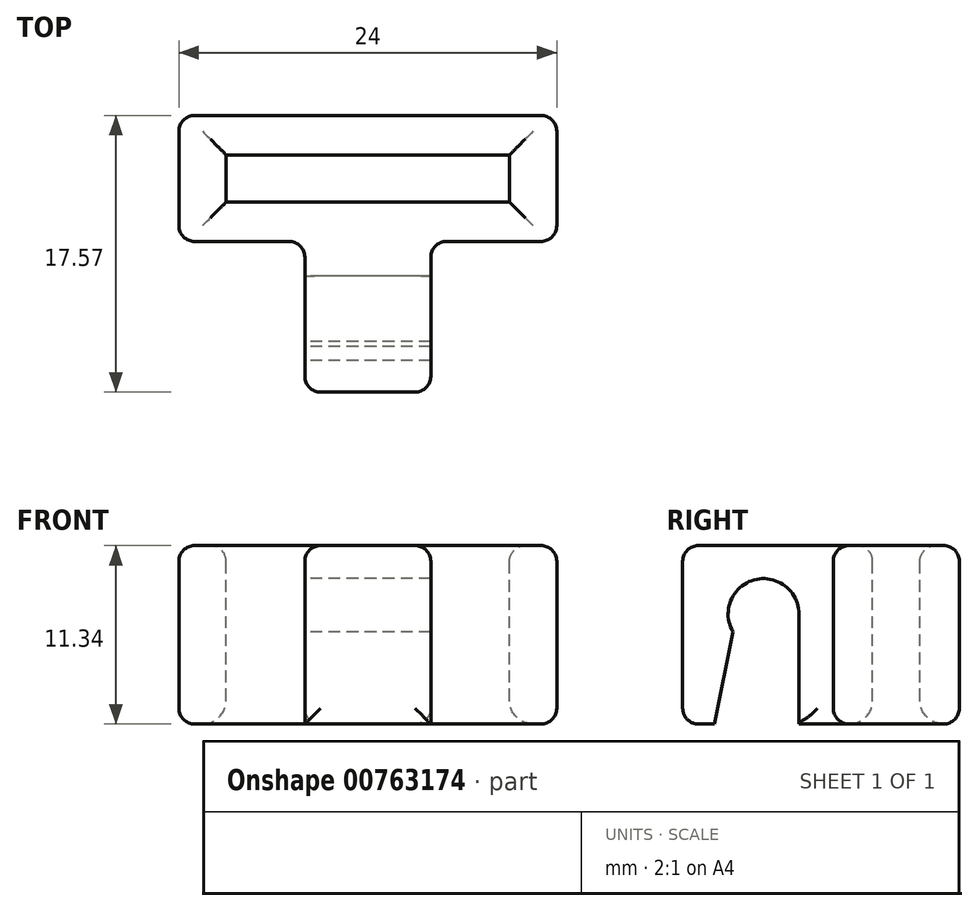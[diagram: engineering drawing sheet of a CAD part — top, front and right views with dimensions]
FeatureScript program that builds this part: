
annotation { "Feature Type Name" : "Feature", "Feature Type Description" : "" }
export const myFeature = defineFeature(function(context is Context, id is Id, definition is map)
    precondition{}
    {
        {
            var Q0;
            Q0=qCreatedBy(makeId("Right.planeOp"),FACE);
            var sketch = newSketch(context, id + "F0", { "sketchPlane" : qUnion([Q0])});
            skArc(sketch, "E0", {"start": v(-16.42, 11.9) * mm, "mid": v(-19.26, 14.08) * mm, "end": v(-20.6, 10.76) * mm});
            skLineSegment(sketch, "E1", {"start": v(-16.42, 11.9) * mm, "end": v(-16.42, 4.92) * mm});
            skLineSegment(sketch, "E2", {"start": v(-20.6, 10.76) * mm, "end": v(-21.78, 4.92) * mm});
            skLineSegment(sketch, "E3", {"start": v(-16.42, 4.92) * mm, "end": v(-14.23, 4.92) * mm});
            skLineSegment(sketch, "E4", {"start": v(-14.23, 4.92) * mm, "end": v(-14.23, 16.26) * mm});
            skLineSegment(sketch, "E5", {"start": v(-14.23, 16.26) * mm, "end": v(-23.8, 16.26) * mm});
            skLineSegment(sketch, "E6", {"start": v(-23.8, 16.26) * mm, "end": v(-23.8, 4.92) * mm});
            skLineSegment(sketch, "E7", {"start": v(-23.8, 4.92) * mm, "end": v(-21.78, 4.92) * mm});
            skSolve(sketch);
        }
        {
            var Q0;
            Q0=makeQuery(id+"F0.imprint","IMPRINT",FACE,{"disambiguationData":[TD([[makeQuery(id+"F0.imprint","IMPRINT",EDGE,{"derivedFrom":sQuery(id+"F0.wireOp",EDGE,"E0")}),-1.0]])]});
            extrude(context, id + "F1", {"entities" : qUnion([Q0]), "depth" : 8 * mm, "offsetDistance" : 25 * mm});
        }
        {
            var Q0;
            Q0=makeQuery(id+"F1.opExtrude","SWEPT_FACE",FACE,{"disambiguationData":[OSD([sQuery(id+"F0.wireOp",EDGE,"E4")])]});
            var sketch = newSketch(context, id + "F2", { "sketchPlane" : qUnion([Q0])});
            skLineSegment(sketch, "E8", {"start": v(-16, 4.92) * mm, "end": v(-16, 16.26) * mm});
            skLineSegment(sketch, "E9", {"start": v(-16, 16.26) * mm, "end": v(8, 16.26) * mm});
            skLineSegment(sketch, "E10", {"start": v(8, 16.26) * mm, "end": v(8, 4.92) * mm});
            skLineSegment(sketch, "E11", {"start": v(-16, 4.92) * mm, "end": v(8, 4.92) * mm});
            skSolve(sketch);
        }
        {
            var Q0;
            Q0 = qSketchRegion(id + "F2", true);
            extrude(context, id + "F3", {"entities" : qUnion([Q0]), "operationType" : NewBodyOperationType.ADD, "depth" : 8 * mm, "offsetDistance" : 25 * mm});
        }
        {
            var Q0;
            Q0=makeQuery(id+"F3.boolean.opBoolean","MERGE",FACE,{"derivedFrom":[makeQuery(id+"F1.opExtrude","SWEPT_FACE",FACE,{"disambiguationData":[OSD([sQuery(id+"F0.wireOp",EDGE,"E5")])]}),makeQuery(id+"F3.opExtrude","SWEPT_FACE",FACE,{"disambiguationData":[OSD([sQuery(id+"F2.wireOp",EDGE,"E9")])]})]});
            var sketch = newSketch(context, id + "F4", { "sketchPlane" : qUnion([Q0])});
            skLineSegment(sketch, "E12", {"start": v(13, -11.73) * mm, "end": v(13, -8.73) * mm});
            skLineSegment(sketch, "E13", {"start": v(13, -8.73) * mm, "end": v(-5, -8.73) * mm});
            skLineSegment(sketch, "E14", {"start": v(-5, -8.73) * mm, "end": v(-5, -11.73) * mm});
            skLineSegment(sketch, "E15", {"start": v(-5, -11.73) * mm, "end": v(13, -11.73) * mm});
            skSolve(sketch);
        }
        {
            var Q0;
            Q0=makeQuery(id+"F4.imprint","IMPRINT",FACE,{"disambiguationData":[TD([[makeQuery(id+"F4.imprint","IMPRINT",EDGE,{"derivedFrom":sQuery(id+"F4.wireOp",EDGE,"E12")}),1.0]])]});
            extrude(context, id + "F5", {"entities" : qUnion([Q0]), "operationType" : NewBodyOperationType.REMOVE, "endBound" : BoundingType.THROUGH_ALL, "oppositeDirection" : true, "depth" : 25 * mm, "offsetDistance" : 25 * mm});
        }
        {
            var Q0;
            Q0=makeQuery(id+"F3.boolean.opBoolean","MERGE",FACE,{"derivedFrom":[makeQuery(id+"F1.opExtrude","SWEPT_FACE",FACE,{"disambiguationData":[OSD([sQuery(id+"F0.wireOp",EDGE,"E5")])]}),makeQuery(id+"F3.opExtrude","SWEPT_FACE",FACE,{"disambiguationData":[OSD([sQuery(id+"F2.wireOp",EDGE,"E9")])]})]});
            var Q1;
            Q1=makeQuery(id+"F3.opExtrude","SWEPT_FACE",FACE,{"disambiguationData":[OSD([sQuery(id+"F2.wireOp",EDGE,"E8")])]});
            var Q2;
            Q2=makeQuery(id+"F3.opExtrude","CAP_FACE",FACE,{"disambiguationData":[OSD([sQuery(id+"F2.wireOp",EDGE,"E8"),sQuery(id+"F2.wireOp",EDGE,"E9"),sQuery(id+"F2.wireOp",EDGE,"E10"),sQuery(id+"F2.wireOp",EDGE,"E11")])],"isStart":false});
            var Q3;
            Q3=makeQuery(id+"F3.opExtrude","SWEPT_FACE",FACE,{"disambiguationData":[OSD([sQuery(id+"F2.wireOp",EDGE,"E10")])]});
            var Q4;
            {var subQ2=sQuery(id+"F2.wireOp",EDGE,"E10");var subQ3=sQuery(id+"F2.wireOp",EDGE,"E9");var subQ4=sQuery(id+"F2.wireOp",EDGE,"E11");Q4=makeQuery(id+"F3.boolean.opBoolean","SPLIT",FACE,{"disambiguationData":[TD([makeQuery(id+"F3.opExtrude","SWEPT_FACE",FACE,{"disambiguationData":[OSD([subQ2])]})])],"derivedFrom":makeQuery(id+"F3.opExtrude","CAP_FACE",FACE,{"disambiguationData":[OSD([sQuery(id+"F2.wireOp",EDGE,"E8"),subQ3,subQ2,subQ4])],"isStart":true})});}
            var Q5;
            {var subQ0=sQuery(id+"F2.wireOp",EDGE,"E8");var subQ3=sQuery(id+"F2.wireOp",EDGE,"E9");var subQ4=sQuery(id+"F2.wireOp",EDGE,"E11");Q5=makeQuery(id+"F3.boolean.opBoolean","SPLIT",FACE,{"disambiguationData":[TD([makeQuery(id+"F3.opExtrude","SWEPT_FACE",FACE,{"disambiguationData":[OSD([subQ0])]})])],"derivedFrom":makeQuery(id+"F3.opExtrude","CAP_FACE",FACE,{"disambiguationData":[OSD([subQ0,subQ3,sQuery(id+"F2.wireOp",EDGE,"E10"),subQ4])],"isStart":true})});}
            var Q6;
            Q6=makeQuery(id+"F1.opExtrude","SWEPT_FACE",FACE,{"disambiguationData":[OSD([sQuery(id+"F0.wireOp",EDGE,"E6")])]});
            fillet(context, id + "F6", {"entities" : qUnion([Q0, Q1, Q2, Q3, Q4, Q5, Q6]), "radius" : 1 * mm, "tangentPropagation" : true, "allowEdgeOverflow" : false});
        }
        {
            var Q0;
            Q0=makeQuery(id+"F5.boolean.opBoolean","INTERSECT",EDGE,{"derivedFrom":[makeQuery(id+"F3.boolean.opBoolean","MERGE",FACE,{"derivedFrom":[makeQuery(id+"F1.opExtrude","SWEPT_FACE",FACE,{"disambiguationData":[OSD([sQuery(id+"F0.wireOp",EDGE,"E3")])]}),makeQuery(id+"F3.opExtrude","SWEPT_FACE",FACE,{"disambiguationData":[OSD([sQuery(id+"F2.wireOp",EDGE,"E11")])]})]}),makeQuery(id+"F5.opExtrude","SWEPT_FACE",FACE,{"disambiguationData":[OSD([sQuery(id+"F4.wireOp",EDGE,"E14")])]})]});
            var Q1;
            Q1=makeQuery(id+"F5.boolean.opBoolean","INTERSECT",EDGE,{"derivedFrom":[makeQuery(id+"F3.boolean.opBoolean","MERGE",FACE,{"derivedFrom":[makeQuery(id+"F1.opExtrude","SWEPT_FACE",FACE,{"disambiguationData":[OSD([sQuery(id+"F0.wireOp",EDGE,"E3")])]}),makeQuery(id+"F3.opExtrude","SWEPT_FACE",FACE,{"disambiguationData":[OSD([sQuery(id+"F2.wireOp",EDGE,"E11")])]})]}),makeQuery(id+"F5.opExtrude","SWEPT_FACE",FACE,{"disambiguationData":[OSD([sQuery(id+"F4.wireOp",EDGE,"E15")])]})]});
            var Q2;
            Q2=makeQuery(id+"F5.boolean.opBoolean","INTERSECT",EDGE,{"derivedFrom":[makeQuery(id+"F3.boolean.opBoolean","MERGE",FACE,{"derivedFrom":[makeQuery(id+"F1.opExtrude","SWEPT_FACE",FACE,{"disambiguationData":[OSD([sQuery(id+"F0.wireOp",EDGE,"E3")])]}),makeQuery(id+"F3.opExtrude","SWEPT_FACE",FACE,{"disambiguationData":[OSD([sQuery(id+"F2.wireOp",EDGE,"E11")])]})]}),makeQuery(id+"F5.opExtrude","SWEPT_FACE",FACE,{"disambiguationData":[OSD([sQuery(id+"F4.wireOp",EDGE,"E13")])]})]});
            var Q3;
            Q3=makeQuery(id+"F5.boolean.opBoolean","INTERSECT",EDGE,{"derivedFrom":[makeQuery(id+"F3.boolean.opBoolean","MERGE",FACE,{"derivedFrom":[makeQuery(id+"F1.opExtrude","SWEPT_FACE",FACE,{"disambiguationData":[OSD([sQuery(id+"F0.wireOp",EDGE,"E3")])]}),makeQuery(id+"F3.opExtrude","SWEPT_FACE",FACE,{"disambiguationData":[OSD([sQuery(id+"F2.wireOp",EDGE,"E11")])]})]}),makeQuery(id+"F5.opExtrude","SWEPT_FACE",FACE,{"disambiguationData":[OSD([sQuery(id+"F4.wireOp",EDGE,"E12")])]})]});
            fillet(context, id + "F7", {"entities" : qUnion([Q0, Q1, Q2, Q3]), "radius" : 1.5 * mm, "tangentPropagation" : true, "allowEdgeOverflow" : false});
        }
    });
